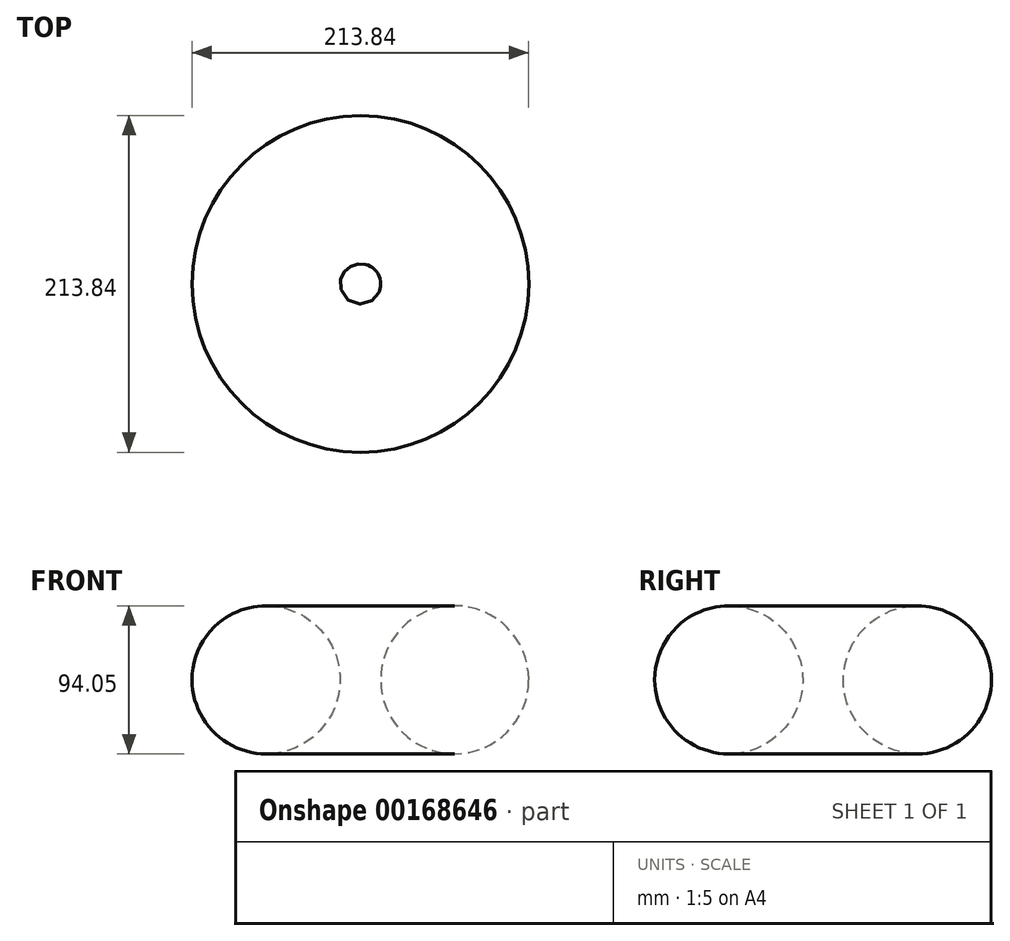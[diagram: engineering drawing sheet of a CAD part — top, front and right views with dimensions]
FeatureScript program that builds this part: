
annotation { "Feature Type Name" : "Feature", "Feature Type Description" : "" }
export const myFeature = defineFeature(function(context is Context, id is Id, definition is map)
    precondition{}
    {
        {
            var Q0;
            Q0=qCreatedBy(makeId("Front.planeOp"),FACE);
            var sketch = newSketch(context, id + "F0", { "sketchPlane" : qUnion([Q0])});
            skCircle(sketch, "E0", {"center": v(-8.2, 8.2) * mm, "radius": 47.03 * mm});
            skLineSegment(sketch, "E1", {"start": v(51.7, 49.02) * mm, "end": v(51.7, -46.64) * mm, "construction": true});
            skSolve(sketch);
        }
        {
            var Q0;
            Q0=makeQuery(id+"F0.imprint","IMPRINT",FACE,{"disambiguationData":[TD([[makeQuery(id+"F0.imprint","IMPRINT",EDGE,{"derivedFrom":sQuery(id+"F0.wireOp",EDGE,"E0")}),1.0]])]});
            var Q1;
            Q1=sQuery(id+"F0.wireOp",EDGE,"E1");
            revolve(context, id + "F1", {"entities" : qUnion([Q0]), "axis" : qUnion([Q1]), "revolveType" : RevolveType.FULL});
        }
    });
